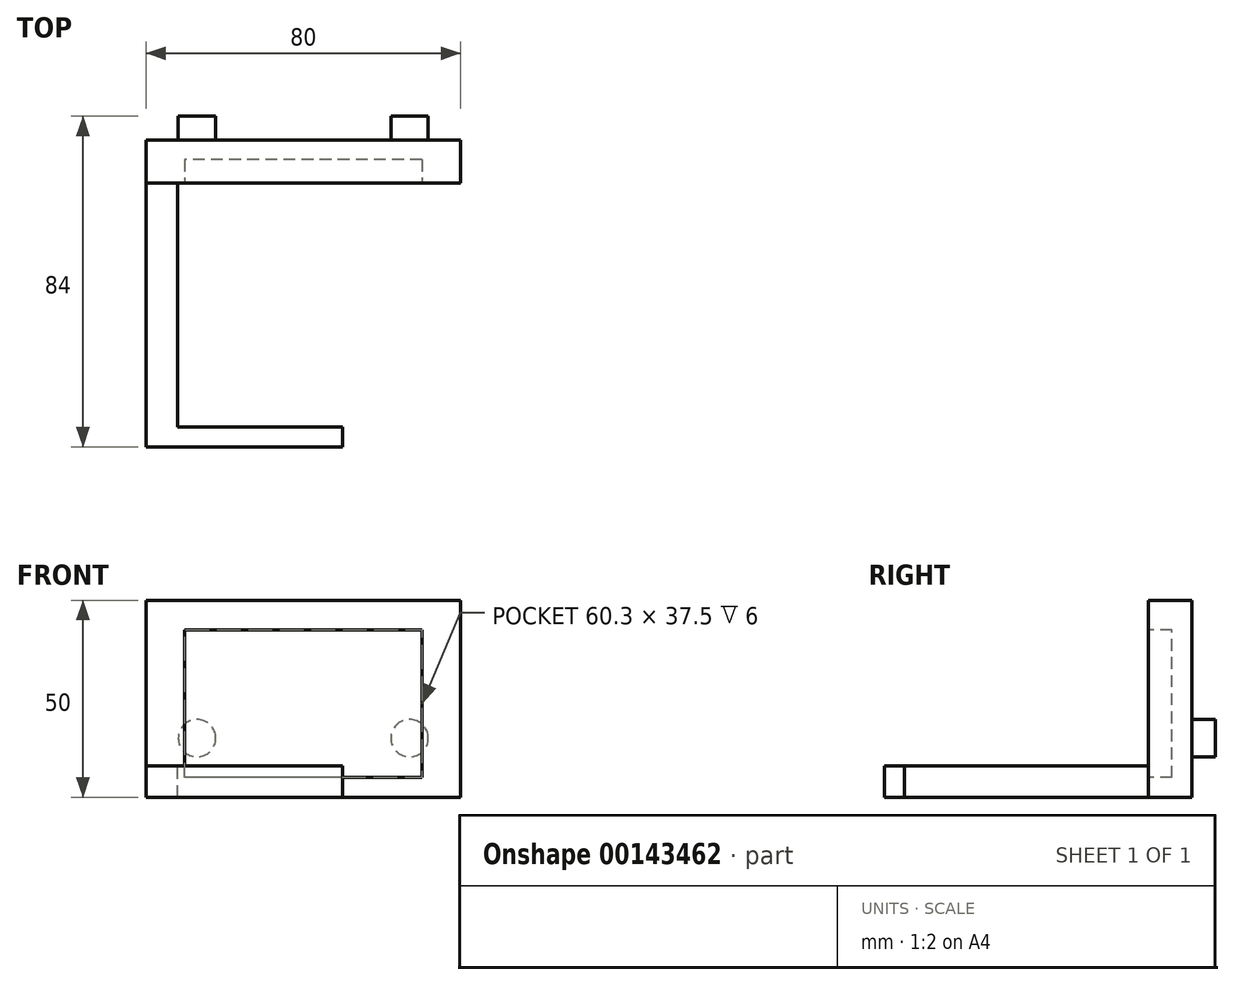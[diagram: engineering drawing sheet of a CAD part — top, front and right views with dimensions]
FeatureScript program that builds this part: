
annotation { "Feature Type Name" : "Feature", "Feature Type Description" : "" }
export const myFeature = defineFeature(function(context is Context, id is Id, definition is map)
    precondition{}
    {
        {
            var Q0;
            Q0=qCreatedBy(makeId("Front.planeOp"),FACE);
            var sketch = newSketch(context, id + "F0", { "sketchPlane" : qUnion([Q0])});
            skCircle(sketch, "E0", {"center": v(-27, 0) * mm, "radius": 4.75 * mm});
            skCircle(sketch, "E1", {"center": v(27, 0) * mm, "radius": 4.75 * mm});
            skSolve(sketch);
        }
        {
            var Q0;
            Q0=makeQuery(id+"F0.imprint","IMPRINT",FACE,{"disambiguationData":[TD([[makeQuery(id+"F0.imprint","IMPRINT",EDGE,{"derivedFrom":sQuery(id+"F0.wireOp",EDGE,"E0")}),1.0]])]});
            var Q1;
            Q1=makeQuery(id+"F0.imprint","IMPRINT",FACE,{"disambiguationData":[TD([[makeQuery(id+"F0.imprint","IMPRINT",EDGE,{"derivedFrom":sQuery(id+"F0.wireOp",EDGE,"E1")}),1.0]])]});
            extrude(context, id + "F1", {"entities" : qUnion([Q0, Q1]), "depth" : 6 * mm});
        }
        {
            var Q0;
            Q0=makeQuery(id+"F1.opExtrude","CAP_FACE",FACE,{"disambiguationData":[OSD([sQuery(id+"F0.wireOp",EDGE,"E0")])],"isStart":false});
            var sketch = newSketch(context, id + "F2", { "sketchPlane" : qUnion([Q0])});
            skLineSegment(sketch, "E2.top", {"start": v(40, -15) * mm, "end": v(-40, -15) * mm});
            skLineSegment(sketch, "E2.left", {"start": v(40, 15) * mm, "end": v(40, -15) * mm});
            skLineSegment(sketch, "E2.right", {"start": v(-40, 15) * mm, "end": v(-40, -15) * mm});
            skPoint(sketch, "E2.middle", {"position": v(0, 0) * mm});
            skLineSegment(sketch, "E3", {"start": v(-40, 15) * mm, "end": v(-40, 35) * mm});
            skLineSegment(sketch, "E4", {"start": v(40, 15) * mm, "end": v(40, 35) * mm});
            skLineSegment(sketch, "E5", {"start": v(40, 35) * mm, "end": v(-40, 35) * mm});
            skSolve(sketch);
        }
        {
            var Q0;
            Q0=makeQuery(id+"F2.imprint","IMPRINT",FACE,{"disambiguationData":[TD([[makeQuery(id+"F2.imprint","IMPRINT",EDGE,{"derivedFrom":makeQuery(id+"F1.opExtrude","CAP_EDGE",EDGE,{"disambiguationData":[OSD([sQuery(id+"F0.wireOp",EDGE,"E0")])],"isStart":false})}),1.0]])]});
            var Q1;
            Q1=makeQuery(id+"F2.imprint","IMPRINT",FACE,{"disambiguationData":[TD([[makeQuery(id+"F2.imprint","IMPRINT",EDGE,{"derivedFrom":sQuery(id+"F2.wireOp",EDGE,"E2.top")}),-1.0]])]});
            extrude(context, id + "F3", {"entities" : qUnion([Q0, Q1]), "depth" : 11 * mm});
        }
        {
            var Q0;
            Q0=makeQuery(id+"F3.opExtrude","CAP_FACE",FACE,{"disambiguationData":[OSD([sQuery(id+"F2.wireOp",EDGE,"E2.top"),sQuery(id+"F2.wireOp",EDGE,"E2.left"),sQuery(id+"F2.wireOp",EDGE,"E2.right"),sQuery(id+"F2.wireOp",EDGE,"E3"),sQuery(id+"F2.wireOp",EDGE,"E4"),sQuery(id+"F2.wireOp",EDGE,"E5")])],"isStart":false});
            var sketch = newSketch(context, id + "F4", { "sketchPlane" : qUnion([Q0])});
            skLineSegment(sketch, "E6.bottom", {"start": v(30.15, -10) * mm, "end": v(-30.15, -10) * mm});
            skLineSegment(sketch, "E6.top", {"start": v(30.15, 27.5) * mm, "end": v(-30.15, 27.5) * mm});
            skLineSegment(sketch, "E6.left", {"start": v(30.15, -10) * mm, "end": v(30.15, 27.5) * mm});
            skLineSegment(sketch, "E6.right", {"start": v(-30.15, -10) * mm, "end": v(-30.15, 27.5) * mm});
            skLineSegment(sketch, "E7.0.0", {"start": v(40, -15) * mm, "end": v(-40, -15) * mm});
            skLineSegment(sketch, "E7.0.1", {"start": v(-40, -15) * mm, "end": v(-40, 35) * mm});
            skLineSegment(sketch, "E7.0.2", {"start": v(-40, 35) * mm, "end": v(40, 35) * mm});
            skLineSegment(sketch, "E7.0.3", {"start": v(40, 35) * mm, "end": v(40, -15) * mm});
            skSolve(sketch);
        }
        {
            var Q0;
            Q0=makeQuery(id+"F4.imprint","IMPRINT",FACE,{"disambiguationData":[TD([[makeQuery(id+"F4.imprint","IMPRINT",EDGE,{"derivedFrom":sQuery(id+"F4.wireOp",EDGE,"E6.bottom")}),-1.0]])]});
            extrude(context, id + "F5", {"entities" : qUnion([Q0]), "operationType" : NewBodyOperationType.REMOVE, "oppositeDirection" : true, "depth" : 6 * mm});
        }
        {
            var Q0;
            Q0=makeQuery(id+"F3.opExtrude","CAP_FACE",FACE,{"disambiguationData":[OSD([sQuery(id+"F2.wireOp",EDGE,"E2.top"),sQuery(id+"F2.wireOp",EDGE,"E2.left"),sQuery(id+"F2.wireOp",EDGE,"E2.right"),sQuery(id+"F2.wireOp",EDGE,"E3"),sQuery(id+"F2.wireOp",EDGE,"E4"),sQuery(id+"F2.wireOp",EDGE,"E5")])],"isStart":false});
            var sketch = newSketch(context, id + "F6", { "sketchPlane" : qUnion([Q0])});
            skLineSegment(sketch, "E8.bottom", {"start": v(-40, -15) * mm, "end": v(-32, -15) * mm});
            skLineSegment(sketch, "E8.top", {"start": v(-40, -7) * mm, "end": v(-32, -7) * mm});
            skLineSegment(sketch, "E8.left", {"start": v(-40, -15) * mm, "end": v(-40, -7) * mm});
            skLineSegment(sketch, "E8.right", {"start": v(-32, -15) * mm, "end": v(-32, -7) * mm});
            skSolve(sketch);
        }
        {
            var Q0;
            Q0=makeQuery(id+"F6.imprint","IMPRINT",FACE,{"disambiguationData":[TD([[makeQuery(id+"F6.imprint","IMPRINT",EDGE,{"derivedFrom":sQuery(id+"F6.wireOp",EDGE,"E8.bottom")}),-1.0]])]});
            extrude(context, id + "F7", {"entities" : qUnion([Q0]), "operationType" : NewBodyOperationType.ADD, "depth" : 67 * mm});
        }
        {
            var Q0;
            Q0=makeQuery(id+"F7.opExtrude","CAP_FACE",FACE,{"disambiguationData":[OSD([sQuery(id+"F6.wireOp",EDGE,"E8.bottom"),sQuery(id+"F6.wireOp",EDGE,"E8.top"),sQuery(id+"F6.wireOp",EDGE,"E8.left"),sQuery(id+"F6.wireOp",EDGE,"E8.right")])],"isStart":false});
            var sketch = newSketch(context, id + "F8", { "sketchPlane" : qUnion([Q0])});
            skLineSegment(sketch, "E9.0.0", {"start": v(-32, -7) * mm, "end": v(-40, -7) * mm});
            skLineSegment(sketch, "E9.0.1", {"start": v(-40, -7) * mm, "end": v(-40, -15) * mm});
            skLineSegment(sketch, "E9.0.2", {"start": v(-40, -15) * mm, "end": v(-32, -15) * mm});
            skLineSegment(sketch, "E9.0.3", {"start": v(-32, -15) * mm, "end": v(-32, -7) * mm});
            skLineSegment(sketch, "E10.bottom", {"start": v(-40, -15) * mm, "end": v(10, -15) * mm});
            skLineSegment(sketch, "E10.top", {"start": v(-40, -7) * mm, "end": v(10, -7) * mm});
            skLineSegment(sketch, "E10.left", {"start": v(-40, -15) * mm, "end": v(-40, -7) * mm});
            skLineSegment(sketch, "E10.right", {"start": v(10, -15) * mm, "end": v(10, -7) * mm});
            skSolve(sketch);
        }
        {
            var Q0;
            {var subQ0=sQuery(id+"F8.wireOp",EDGE,"E9.0.3");Q0=makeQuery(id+"F8.imprint","IMPRINT",FACE,{"disambiguationData":[TD([[makeQuery(id+"F8.imprint","IMPRINT",EDGE,{"derivedFrom":subQ0}),-1.0]])]});}
            extrude(context, id + "F9", {"entities" : qUnion([Q0]), "operationType" : NewBodyOperationType.ADD, "oppositeDirection" : true, "depth" : 5 * mm});
        }
    });
